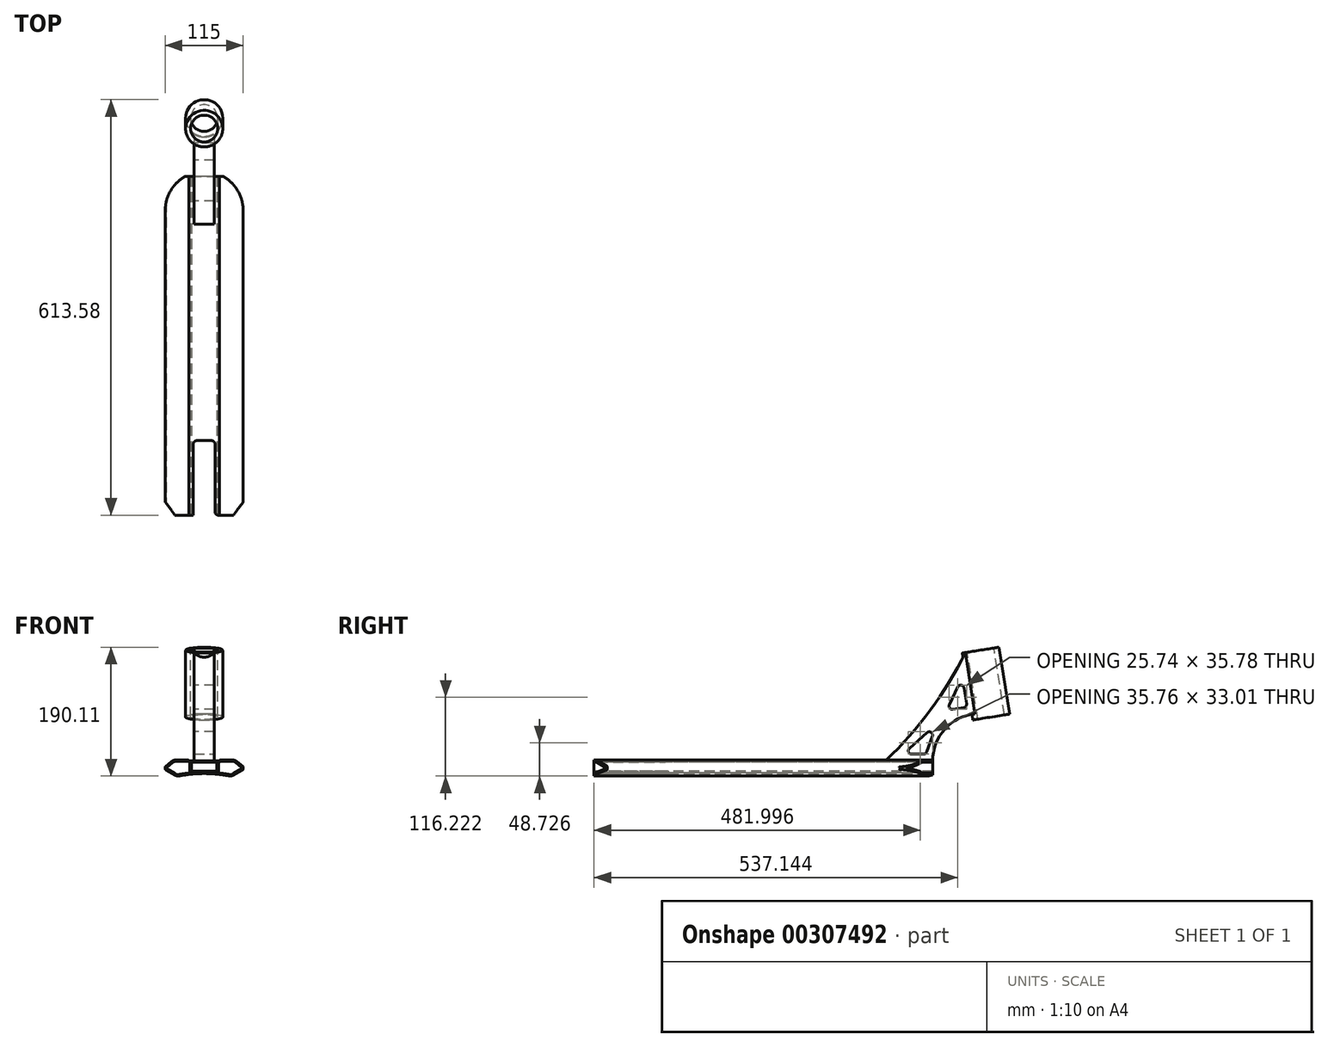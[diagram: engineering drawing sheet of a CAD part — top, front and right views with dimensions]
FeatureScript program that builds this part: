
annotation { "Feature Type Name" : "Feature", "Feature Type Description" : "" }
export const myFeature = defineFeature(function(context is Context, id is Id, definition is map)
    precondition{}
    {
        {
            var Q0;
            Q0=qCreatedBy(makeId("Front.planeOp"),FACE);
            var sketch = newSketch(context, id + "F0", { "sketchPlane" : qUnion([Q0])});
            skLineSegment(sketch, "E0", {"start": v(0, 0) * mm, "end": v(0, 24.16) * mm, "construction": true});
            skLineSegment(sketch, "E1", {"start": v(0, 0) * mm, "end": v(22.5, 0) * mm});
            skLineSegment(sketch, "E2", {"start": v(22.5, 0) * mm, "end": v(22.5, 1.3) * mm});
            skLineSegment(sketch, "E3", {"start": v(22.5, 1.3) * mm, "end": v(45.58, 1.3) * mm});
            skLineSegment(sketch, "E4", {"start": v(45.58, 1.3) * mm, "end": v(57.5, -8.7) * mm});
            skLineSegment(sketch, "E5", {"start": v(57.5, -8.7) * mm, "end": v(57.5, -12.7) * mm});
            skLineSegment(sketch, "E6", {"start": v(57.5, -12.7) * mm, "end": v(40.18, -22.7) * mm});
            skLineSegment(sketch, "E7.MirrorCS", {"start": v(0, 0) * mm, "end": v(-22.5, 0) * mm});
            skLineSegment(sketch, "E8.MirrorCS", {"start": v(-22.5, 1.3) * mm, "end": v(-45.58, 1.3) * mm});
            skLineSegment(sketch, "E9.MirrorCS", {"start": v(-22.5, 0) * mm, "end": v(-22.5, 1.3) * mm});
            skLineSegment(sketch, "E10.MirrorCS", {"start": v(-45.58, 1.3) * mm, "end": v(-57.5, -8.7) * mm});
            skLineSegment(sketch, "E11.MirrorCS", {"start": v(-57.5, -8.7) * mm, "end": v(-57.5, -12.7) * mm});
            skLineSegment(sketch, "E12.MirrorCS", {"start": v(-57.5, -12.7) * mm, "end": v(-40.18, -22.7) * mm});
            skArc(sketch, "E13", {"start": v(40.18, -22.7) * mm, "mid": v(0, -18.62) * mm, "end": v(-40.18, -22.7) * mm});
            skSolve(sketch);
        }
        {
            var Q0;
            Q0 = qSketchRegion(id + "F0", true);
            extrude(context, id + "F1", {"entities" : qUnion([Q0]), "endBound" : BoundingType.SYMMETRIC, "depth" : 500 * mm});
        }
        {
            var Q0;
            Q0=qCreatedBy(makeId("Front.planeOp"),FACE);
            var sketch = newSketch(context, id + "F2", { "sketchPlane" : qUnion([Q0])});
            skLineSegment(sketch, "E14.bottom", {"start": v(-19, -2) * mm, "end": v(19, -2) * mm});
            skLineSegment(sketch, "E14.top", {"start": v(-19, -15) * mm, "end": v(19, -15) * mm});
            skLineSegment(sketch, "E14.left", {"start": v(-19, -2) * mm, "end": v(-19, -15) * mm});
            skLineSegment(sketch, "E14.right", {"start": v(19, -2) * mm, "end": v(19, -15) * mm});
            skSolve(sketch);
        }
        {
            var Q0;
            Q0 = qSketchRegion(id + "F2", true);
            extrude(context, id + "F3", {"entities" : qUnion([Q0]), "operationType" : NewBodyOperationType.REMOVE, "endBound" : BoundingType.SYMMETRIC, "oppositeDirection" : true, "depth" : 500 * mm});
        }
        {
            var Q0;
            Q0=makeQuery(id+"F1.opExtrude","SWEPT_EDGE",EDGE,{"disambiguationData":[OSD([sQuery(id+"F0.wireOp",EDGE,"E8.MirrorCS"),sQuery(id+"F0.wireOp",EDGE,"E9.MirrorCS")])]});
            var Q1;
            Q1=makeQuery(id+"F1.opExtrude","SWEPT_EDGE",EDGE,{"disambiguationData":[OSD([sQuery(id+"F0.wireOp",EDGE,"E2"),sQuery(id+"F0.wireOp",EDGE,"E3")])]});
            fillet(context, id + "F4", {"entities" : qUnion([Q0, Q1]), "radius" : 2 * mm, "tangentPropagation" : true, "allowEdgeOverflow" : false});
        }
        {
            var Q0;
            Q0=makeQuery(id+"F1.opExtrude","SWEPT_EDGE",EDGE,{"disambiguationData":[OSD([sQuery(id+"F0.wireOp",EDGE,"E3"),sQuery(id+"F0.wireOp",EDGE,"E4")])]});
            var Q1;
            Q1=makeQuery(id+"F1.opExtrude","SWEPT_EDGE",EDGE,{"disambiguationData":[OSD([sQuery(id+"F0.wireOp",EDGE,"E6"),sQuery(id+"F0.wireOp",EDGE,"E13")])]});
            var Q2;
            Q2=makeQuery(id+"F1.opExtrude","SWEPT_EDGE",EDGE,{"disambiguationData":[OSD([sQuery(id+"F0.wireOp",EDGE,"E8.MirrorCS"),sQuery(id+"F0.wireOp",EDGE,"E10.MirrorCS")])]});
            var Q3;
            Q3=makeQuery(id+"F1.opExtrude","SWEPT_EDGE",EDGE,{"disambiguationData":[OSD([sQuery(id+"F0.wireOp",EDGE,"E12.MirrorCS"),sQuery(id+"F0.wireOp",EDGE,"E13")])]});
            fillet(context, id + "F5", {"entities" : qUnion([Q0, Q1, Q2, Q3]), "radius" : 9 * mm, "tangentPropagation" : true, "allowEdgeOverflow" : false});
        }
        {
            var Q0;
            Q0=makeQuery(id+"F1.opExtrude","SWEPT_EDGE",EDGE,{"disambiguationData":[OSD([sQuery(id+"F0.wireOp",EDGE,"E4"),sQuery(id+"F0.wireOp",EDGE,"E5")])]});
            var Q1;
            Q1=makeQuery(id+"F1.opExtrude","SWEPT_EDGE",EDGE,{"disambiguationData":[OSD([sQuery(id+"F0.wireOp",EDGE,"E5"),sQuery(id+"F0.wireOp",EDGE,"E6")])]});
            var Q2;
            Q2=makeQuery(id+"F1.opExtrude","SWEPT_EDGE",EDGE,{"disambiguationData":[OSD([sQuery(id+"F0.wireOp",EDGE,"E10.MirrorCS"),sQuery(id+"F0.wireOp",EDGE,"E11.MirrorCS")])]});
            var Q3;
            Q3=makeQuery(id+"F1.opExtrude","SWEPT_EDGE",EDGE,{"disambiguationData":[OSD([sQuery(id+"F0.wireOp",EDGE,"E11.MirrorCS"),sQuery(id+"F0.wireOp",EDGE,"E12.MirrorCS")])]});
            fillet(context, id + "F6", {"entities" : qUnion([Q0, Q1, Q2, Q3]), "radius" : 1 * mm, "tangentPropagation" : true, "allowEdgeOverflow" : false});
        }
        {
            var Q0;
            Q0=makeQuery(id+"F1.opExtrude","CAP_FACE",FACE,{"disambiguationData":[OSD([sQuery(id+"F0.wireOp",EDGE,"E1"),sQuery(id+"F0.wireOp",EDGE,"E2"),sQuery(id+"F0.wireOp",EDGE,"E3"),sQuery(id+"F0.wireOp",EDGE,"E4"),sQuery(id+"F0.wireOp",EDGE,"E5"),sQuery(id+"F0.wireOp",EDGE,"E6"),sQuery(id+"F0.wireOp",EDGE,"E7.MirrorCS"),sQuery(id+"F0.wireOp",EDGE,"E8.MirrorCS"),sQuery(id+"F0.wireOp",EDGE,"E9.MirrorCS"),sQuery(id+"F0.wireOp",EDGE,"E10.MirrorCS"),sQuery(id+"F0.wireOp",EDGE,"E11.MirrorCS"),sQuery(id+"F0.wireOp",EDGE,"E12.MirrorCS"),sQuery(id+"F0.wireOp",EDGE,"E13")])],"isStart":false});
            var sketch = newSketch(context, id + "F7", { "sketchPlane" : qUnion([Q0])});
            skArc(sketch, "E15.0", {"start": v(-37.3, -20.1) * mm, "mid": v(0, -16.62) * mm, "end": v(37.3, -20.1) * mm});
            skArc(sketch, "E15.1", {"start": v(-42.1, -19.28) * mm, "mid": v(-39.78, -20.12) * mm, "end": v(-37.3, -20.1) * mm});
            skLineSegment(sketch, "E15.2", {"start": v(-24.37, -0.7) * mm, "end": v(-42.3, -0.7) * mm});
            skArc(sketch, "E15.3", {"start": v(-42.3, -0.7) * mm, "mid": v(-44.7, -1.12) * mm, "end": v(-46.8, -2.34) * mm});
            skLineSegment(sketch, "E15.4", {"start": v(-46.8, -2.34) * mm, "end": v(-55.76, -9.85) * mm});
            skLineSegment(sketch, "E15.5", {"start": v(-55.61, -11.48) * mm, "end": v(-42.1, -19.28) * mm});
            skPoint(sketch, "E16.visualSharp", {"position": v(-56.85, -10.77) * mm});
            skArc(sketch, "E16.filletArc", {"start": v(-55.76, -9.85) * mm, "mid": v(-56.1, -10.7) * mm, "end": v(-55.61, -11.48) * mm});
            skLineSegment(sketch, "E17", {"start": v(-21, -17.72) * mm, "end": v(-21, -2) * mm});
            skLineSegment(sketch, "E18", {"start": v(-21, -2) * mm, "end": v(-22.5, -2) * mm});
            skArc(sketch, "E19", {"start": v(-22.5, -2) * mm, "mid": v(-23.23, -1.06) * mm, "end": v(-24.37, -0.7) * mm});
            skLineSegment(sketch, "E20.MirrorCS", {"start": v(55.61, -11.48) * mm, "end": v(42.1, -19.28) * mm});
            skArc(sketch, "E21.MirrorCS", {"start": v(42.1, -19.28) * mm, "mid": v(39.78, -20.12) * mm, "end": v(37.3, -20.1) * mm});
            skArc(sketch, "E22.MirrorCS", {"start": v(55.76, -9.85) * mm, "mid": v(56.1, -10.7) * mm, "end": v(55.61, -11.48) * mm});
            skLineSegment(sketch, "E23.MirrorCS", {"start": v(46.8, -2.34) * mm, "end": v(55.76, -9.85) * mm});
            skArc(sketch, "E24.MirrorCS", {"start": v(42.3, -0.7) * mm, "mid": v(44.7, -1.12) * mm, "end": v(46.8, -2.34) * mm});
            skLineSegment(sketch, "E25.MirrorCS", {"start": v(24.37, -0.7) * mm, "end": v(42.3, -0.7) * mm});
            skArc(sketch, "E26.MirrorCS", {"start": v(22.5, -2) * mm, "mid": v(23.23, -1.06) * mm, "end": v(24.37, -0.7) * mm});
            skLineSegment(sketch, "E27.MirrorCS", {"start": v(21, -2) * mm, "end": v(22.5, -2) * mm});
            skLineSegment(sketch, "E28.MirrorCS", {"start": v(21, -17.72) * mm, "end": v(21, -2) * mm});
            skArc(sketch, "E29.MirrorCS", {"start": v(37.3, -20.1) * mm, "mid": v(0, -16.62) * mm, "end": v(-37.3, -20.1) * mm});
            skPoint(sketch, "E30.0.15.end.orphan", {"position": v(-24.37, 1.3) * mm});
            skPoint(sketch, "E30.0.14.end.orphan", {"position": v(-22.5, 0) * mm});
            skPoint(sketch, "E30.0.13.end.orphan", {"position": v(22.5, 0) * mm});
            skPoint(sketch, "E30.0.12.end.orphan", {"position": v(24.37, 1.3) * mm});
            skPoint(sketch, "E30.0.11.end.orphan", {"position": v(42.3, 1.3) * mm});
            skPoint(sketch, "E30.0.10.end.orphan", {"position": v(48.1, -0.8) * mm});
            skPoint(sketch, "E30.0.9.end.orphan", {"position": v(57.14, -8.4) * mm});
            skPoint(sketch, "E30.0.8.end.orphan", {"position": v(57.5, -9.17) * mm});
            skPoint(sketch, "E30.0.7.end.orphan", {"position": v(57.5, -12.12) * mm});
            skPoint(sketch, "E30.0.6.end.orphan", {"position": v(57, -12.99) * mm});
            skPoint(sketch, "E30.0.5.end.orphan", {"position": v(43.1, -21.01) * mm});
            skPoint(sketch, "E30.0.4.end.orphan", {"position": v(36.94, -22.06) * mm});
            skPoint(sketch, "E30.0.3.end.orphan", {"position": v(-36.94, -22.06) * mm});
            skPoint(sketch, "E30.0.2.end.orphan", {"position": v(-43.1, -21.01) * mm});
            skPoint(sketch, "E30.0.1.end.orphan", {"position": v(-57, -12.99) * mm});
            skPoint(sketch, "E30.0.0.end.orphan", {"position": v(-57.5, -12.12) * mm});
            skPoint(sketch, "E30.0.19.end.orphan", {"position": v(-57.5, -9.17) * mm});
            skPoint(sketch, "E30.0.18.end.orphan", {"position": v(-57.14, -8.4) * mm});
            skPoint(sketch, "E30.0.17.end.orphan", {"position": v(-48.1, -0.8) * mm});
            skPoint(sketch, "E30.0.17.start.orphan", {"position": v(-42.3, 1.3) * mm});
            skSolve(sketch);
        }
        {
            var Q0;
            Q0=makeQuery(id+"F7.imprint","IMPRINT",FACE,{"disambiguationData":[TD([[makeQuery(id+"F7.imprint","IMPRINT",EDGE,{"derivedFrom":sQuery(id+"F7.wireOp",EDGE,"E20.MirrorCS")}),-1.0]])]});
            var Q1;
            {var subQ0=sQuery(id+"F7.wireOp",EDGE,"E15.1");Q1=makeQuery(id+"F7.imprint","IMPRINT",FACE,{"disambiguationData":[TD([[makeQuery(id+"F7.imprint","IMPRINT",EDGE,{"derivedFrom":subQ0}),1.0]])]});}
            extrude(context, id + "F8", {"entities" : qUnion([Q0, Q1]), "operationType" : NewBodyOperationType.REMOVE, "endBound" : BoundingType.THROUGH_ALL, "oppositeDirection" : true, "depth" : 25 * mm});
        }
        {
            var Q0;
            Q0=qCreatedBy(makeId("Top.planeOp"),FACE);
            var sketch = newSketch(context, id + "F9", { "sketchPlane" : qUnion([Q0])});
            skArc(sketch, "E31", {"start": v(57.5, 200) * mm, "mid": v(0, 257.5) * mm, "end": v(-57.5, 200) * mm});
            skLineSegment(sketch, "E32", {"start": v(-57.5, 200) * mm, "end": v(-57.5, 280) * mm});
            skLineSegment(sketch, "E33", {"start": v(57.5, 200) * mm, "end": v(57.5, 280) * mm});
            skLineSegment(sketch, "E34", {"start": v(-57.5, 280) * mm, "end": v(57.5, 280) * mm});
            skSolve(sketch);
        }
        {
            var Q0;
            Q0 = qSketchRegion(id + "F9", true);
            extrude(context, id + "F10", {"entities" : qUnion([Q0]), "operationType" : NewBodyOperationType.ADD, "depth" : 25 * mm});
        }
        {
            var Q0;
            Q0 = qSketchRegion(id + "F9", true);
            extrude(context, id + "F11", {"entities" : qUnion([Q0]), "operationType" : NewBodyOperationType.REMOVE, "endBound" : BoundingType.THROUGH_ALL, "oppositeDirection" : true, "depth" : 25 * mm, "hasSecondDirection" : true, "secondDirectionBound" : SecondDirectionBoundingType.THROUGH_ALL, "secondDirectionOppositeDirection" : false, "secondDirectionDepth" : 25 * mm});
        }
        {
            var Q0;
            Q0=qCreatedBy(makeId("Top.planeOp"),FACE);
            var sketch = newSketch(context, id + "F12", { "sketchPlane" : qUnion([Q0])});
            skLineSegment(sketch, "E35", {"start": v(-68, -216) * mm, "end": v(-43.3, -250) * mm});
            skLineSegment(sketch, "E36", {"start": v(-43.3, -250) * mm, "end": v(-16, -250) * mm});
            skLineSegment(sketch, "E37", {"start": v(-16, -250) * mm, "end": v(-16, -140) * mm});
            skLineSegment(sketch, "E38", {"start": v(-16, -140) * mm, "end": v(16, -140) * mm});
            skLineSegment(sketch, "E39", {"start": v(16, -140) * mm, "end": v(16, -250) * mm});
            skLineSegment(sketch, "E40", {"start": v(16, -250) * mm, "end": v(43.3, -250) * mm});
            skLineSegment(sketch, "E41", {"start": v(43.3, -250) * mm, "end": v(68, -216) * mm});
            skLineSegment(sketch, "E42", {"start": v(68, -216) * mm, "end": v(68, -346) * mm});
            skLineSegment(sketch, "E43", {"start": v(68, -346) * mm, "end": v(-68, -346) * mm});
            skLineSegment(sketch, "E44", {"start": v(-68, -346) * mm, "end": v(-68, -216) * mm});
            skSolve(sketch);
        }
        {
            var Q0;
            Q0 = qSketchRegion(id + "F12", true);
            extrude(context, id + "F13", {"entities" : qUnion([Q0]), "operationType" : NewBodyOperationType.REMOVE, "endBound" : BoundingType.THROUGH_ALL, "oppositeDirection" : true, "depth" : 25 * mm, "hasSecondDirection" : true, "secondDirectionBound" : SecondDirectionBoundingType.THROUGH_ALL, "secondDirectionOppositeDirection" : false, "secondDirectionDepth" : 25 * mm});
        }
        {
            var Q0;
            {var subQ0=sQuery(id+"F12.wireOp",EDGE,"E38");var subQ1=sQuery(id+"F12.wireOp",EDGE,"E37");Q0=makeQuery(id+"F13.boolean.opBoolean","COPY",EDGE,{"disambiguationData":[TD([makeQuery(id+"F1.opExtrude","SWEPT_FACE",FACE,{"disambiguationData":[OSD([sQuery(id+"F0.wireOp",EDGE,"E13")])]})])],"derivedFrom":makeQuery(id+"F13.opExtrude","SWEPT_EDGE",EDGE,{"disambiguationData":[OSD([subQ1,subQ0])]})});}
            var Q1;
            {var subQ0=sQuery(id+"F12.wireOp",EDGE,"E37");var subQ1=sQuery(id+"F12.wireOp",EDGE,"E38");Q1=makeQuery(id+"F13.boolean.opBoolean","COPY",EDGE,{"disambiguationData":[TD([makeQuery(id+"F3.boolean.opBoolean","COPY",FACE,{"derivedFrom":makeQuery(id+"F3.opExtrude","SWEPT_FACE",FACE,{"disambiguationData":[OSD([sQuery(id+"F2.wireOp",EDGE,"E14.bottom")])]})})])],"derivedFrom":makeQuery(id+"F13.opExtrude","SWEPT_EDGE",EDGE,{"disambiguationData":[OSD([subQ0,subQ1])]})});}
            var Q2;
            {var subQ0=sQuery(id+"F12.wireOp",EDGE,"E38");var subQ1=sQuery(id+"F12.wireOp",EDGE,"E39");Q2=makeQuery(id+"F13.boolean.opBoolean","COPY",EDGE,{"disambiguationData":[TD([makeQuery(id+"F1.opExtrude","SWEPT_FACE",FACE,{"disambiguationData":[OSD([sQuery(id+"F0.wireOp",EDGE,"E13")])]})])],"derivedFrom":makeQuery(id+"F13.opExtrude","SWEPT_EDGE",EDGE,{"disambiguationData":[OSD([subQ0,subQ1])]})});}
            var Q3;
            {var subQ0=sQuery(id+"F12.wireOp",EDGE,"E38");var subQ1=sQuery(id+"F12.wireOp",EDGE,"E39");Q3=makeQuery(id+"F13.boolean.opBoolean","COPY",EDGE,{"disambiguationData":[TD([makeQuery(id+"F3.boolean.opBoolean","COPY",FACE,{"derivedFrom":makeQuery(id+"F3.opExtrude","SWEPT_FACE",FACE,{"disambiguationData":[OSD([sQuery(id+"F2.wireOp",EDGE,"E14.bottom")])]})})])],"derivedFrom":makeQuery(id+"F13.opExtrude","SWEPT_EDGE",EDGE,{"disambiguationData":[OSD([subQ0,subQ1])]})});}
            var Q4;
            {var subQ2=sQuery(id+"F12.wireOp",EDGE,"E39");Q4=makeQuery(id+"F13.boolean.opBoolean","COPY",EDGE,{"disambiguationData":[TD([makeQuery(id+"F3.boolean.opBoolean","COPY",FACE,{"derivedFrom":makeQuery(id+"F3.opExtrude","SWEPT_FACE",FACE,{"disambiguationData":[OSD([sQuery(id+"F2.wireOp",EDGE,"E14.bottom")])]})})])],"derivedFrom":makeQuery(id+"F13.opExtrude","SWEPT_EDGE",EDGE,{"disambiguationData":[OSD([subQ2,sQuery(id+"F12.wireOp",EDGE,"E40")])]})});}
            var Q5;
            {var subQ2=sQuery(id+"F12.wireOp",EDGE,"E37");Q5=makeQuery(id+"F13.boolean.opBoolean","COPY",EDGE,{"disambiguationData":[TD([makeQuery(id+"F3.boolean.opBoolean","COPY",FACE,{"derivedFrom":makeQuery(id+"F3.opExtrude","SWEPT_FACE",FACE,{"disambiguationData":[OSD([sQuery(id+"F2.wireOp",EDGE,"E14.bottom")])]})})])],"derivedFrom":makeQuery(id+"F13.opExtrude","SWEPT_EDGE",EDGE,{"disambiguationData":[OSD([sQuery(id+"F12.wireOp",EDGE,"E36"),subQ2])]})});}
            fillet(context, id + "F14", {"entities" : qUnion([Q0, Q1, Q2, Q3, Q4, Q5]), "radius" : 5 * mm, "tangentPropagation" : true, "allowEdgeOverflow" : false});
        }
        {
            var Q0;
            Q0=qCreatedBy(makeId("Right.planeOp"),FACE);
            var sketch = newSketch(context, id + "F15", { "sketchPlane" : qUnion([Q0])});
            skLineSegment(sketch, "E45", {"start": v(180, 0) * mm, "end": v(250, 0) * mm});
            skArc(sketch, "E46", {"start": v(180, 0) * mm, "mid": v(246.34, 74.62) * mm, "end": v(298.1, 160) * mm});
            skLineSegment(sketch, "E47", {"start": v(298.1, 160) * mm, "end": v(343.53, 167.2) * mm});
            skArc(sketch, "E48", {"start": v(312.42, 69.59) * mm, "mid": v(267.9, 46.74) * mm, "end": v(250, 0) * mm});
            skLineSegment(sketch, "E49", {"start": v(312.42, 69.59) * mm, "end": v(313.74, 61.23) * mm});
            skLineSegment(sketch, "E50", {"start": v(313.74, 61.23) * mm, "end": v(359.18, 68.43) * mm});
            skLineSegment(sketch, "E51", {"start": v(343.53, 167.2) * mm, "end": v(359.18, 68.43) * mm});
            skSolve(sketch);
        }
        {
            var Q0;
            Q0 = qSketchRegion(id + "F15", true);
            extrude(context, id + "F16", {"entities" : qUnion([Q0]), "operationType" : NewBodyOperationType.ADD, "endBound" : BoundingType.SYMMETRIC, "depth" : 30 * mm});
        }
        {
            var Q0;
            Q0=makeQuery(id+"F16.opExtrude","SWEPT_FACE",FACE,{"disambiguationData":[OSD([sQuery(id+"F15.wireOp",EDGE,"E47")])]});
            var sketch = newSketch(context, id + "F17", { "sketchPlane" : qUnion([Q0])});
            skCircle(sketch, "E52", {"center": v(0, 342.46) * mm, "radius": 27.46 * mm});
            skSolve(sketch);
        }
        {
            var Q0;
            Q0 = qSketchRegion(id + "F17", true);
            var Q1;
            Q1=makeQuery(id+"F16.opExtrude","SWEPT_FACE",FACE,{"disambiguationData":[OSD([sQuery(id+"F15.wireOp",EDGE,"E50")])]});
            extrude(context, id + "F18", {"entities" : qUnion([Q0]), "operationType" : NewBodyOperationType.ADD, "endBound" : BoundingType.UP_TO_SURFACE, "oppositeDirection" : true, "endBoundEntityFace" : qUnion([Q1]), "depth" : 25 * mm});
        }
        {
            var Q0;
            Q0=makeQuery(id+"F18.boolean.opBoolean","MERGE",FACE,{"derivedFrom":[makeQuery(id+"F16.opExtrude","SWEPT_FACE",FACE,{"disambiguationData":[OSD([sQuery(id+"F15.wireOp",EDGE,"E47")])]}),makeQuery(id+"F18.opExtrude","CAP_FACE",FACE,{"disambiguationData":[OSD([sQuery(id+"F17.wireOp",EDGE,"E52")])],"isStart":true})]});
            var sketch = newSketch(context, id + "F19", { "sketchPlane" : qUnion([Q0])});
            skPoint(sketch, "E53", {"position": v(0, 342.46) * mm});
            skSolve(sketch);
        }
        {
            var Q0;
            Q0=sQuery(id+"F19.wireOp",VERTEX,"E53");
            var Q1;
            Q1=makeQuery(id+"F1.opExtrude","SWEPT_BODY",BODY,{"disambiguationData":[OSD([sQuery(id+"F0.wireOp",EDGE,"E1"),sQuery(id+"F0.wireOp",EDGE,"E2"),sQuery(id+"F0.wireOp",EDGE,"E3"),sQuery(id+"F0.wireOp",EDGE,"E4"),sQuery(id+"F0.wireOp",EDGE,"E5"),sQuery(id+"F0.wireOp",EDGE,"E6"),sQuery(id+"F0.wireOp",EDGE,"E7.MirrorCS"),sQuery(id+"F0.wireOp",EDGE,"E8.MirrorCS"),sQuery(id+"F0.wireOp",EDGE,"E9.MirrorCS"),sQuery(id+"F0.wireOp",EDGE,"E10.MirrorCS"),sQuery(id+"F0.wireOp",EDGE,"E11.MirrorCS"),sQuery(id+"F0.wireOp",EDGE,"E12.MirrorCS"),sQuery(id+"F0.wireOp",EDGE,"E13")])]});
            hole(context, id + "F20", {"style" : HoleStyle.SIMPLE, "endStyle" : HoleEndStyle.THROUGH, "holeDiameter" : 40 * mm, "isTappedThrough" : true, "tappedDepth" : 12 * mm, "tapClearance" : 3, "locations" : qUnion([Q0]), "scope" : qUnion([Q1])});
        }
        {
            var Q0;
            Q0=makeQuery(id+"F16.opExtrude","CAP_FACE",FACE,{"disambiguationData":[OSD([sQuery(id+"F15.wireOp",EDGE,"E45"),sQuery(id+"F15.wireOp",EDGE,"E46"),sQuery(id+"F15.wireOp",EDGE,"E47"),sQuery(id+"F15.wireOp",EDGE,"E48"),sQuery(id+"F15.wireOp",EDGE,"E49"),sQuery(id+"F15.wireOp",EDGE,"E50"),sQuery(id+"F15.wireOp",EDGE,"E51")])],"isStart":false});
            var sketch = newSketch(context, id + "F21", { "sketchPlane" : qUnion([Q0])});
            skLineSegment(sketch, "E54", {"start": v(293.7, 123.87) * mm, "end": v(270.74, 74.67) * mm});
            skLineSegment(sketch, "E55", {"start": v(270.74, 74.67) * mm, "end": v(300.74, 79.42) * mm});
            skLineSegment(sketch, "E56", {"start": v(300.74, 79.42) * mm, "end": v(293.7, 123.87) * mm});
            skLineSegment(sketch, "E57", {"start": v(256.38, 55) * mm, "end": v(240, 10) * mm});
            skLineSegment(sketch, "E58", {"start": v(240, 10) * mm, "end": v(206, 10) * mm});
            skLineSegment(sketch, "E59", {"start": v(206, 10) * mm, "end": v(256.38, 55) * mm});
            skSolve(sketch);
        }
        {
            var Q0;
            Q0=makeQuery(id+"F21.imprint","IMPRINT",FACE,{"disambiguationData":[TD([[makeQuery(id+"F21.imprint","IMPRINT",EDGE,{"derivedFrom":sQuery(id+"F21.wireOp",EDGE,"E57")}),-1.0]])]});
            var Q1;
            Q1=makeQuery(id+"F21.imprint","IMPRINT",FACE,{"disambiguationData":[TD([[makeQuery(id+"F21.imprint","IMPRINT",EDGE,{"derivedFrom":sQuery(id+"F21.wireOp",EDGE,"E54")}),1.0]])]});
            extrude(context, id + "F22", {"entities" : qUnion([Q0, Q1]), "operationType" : NewBodyOperationType.REMOVE, "endBound" : BoundingType.THROUGH_ALL, "oppositeDirection" : true, "depth" : 25 * mm});
        }
        {
            var Q0;
            Q0=makeQuery(id+"F22.boolean.opBoolean","COPY",EDGE,{"derivedFrom":makeQuery(id+"F22.opExtrude","SWEPT_EDGE",EDGE,{"disambiguationData":[OSD([sQuery(id+"F21.wireOp",EDGE,"E57"),sQuery(id+"F21.wireOp",EDGE,"E58")])]})});
            var Q1;
            Q1=makeQuery(id+"F22.boolean.opBoolean","COPY",EDGE,{"derivedFrom":makeQuery(id+"F22.opExtrude","SWEPT_EDGE",EDGE,{"disambiguationData":[OSD([sQuery(id+"F21.wireOp",EDGE,"E55"),sQuery(id+"F21.wireOp",EDGE,"E56")])]})});
            var Q2;
            Q2=makeQuery(id+"F22.boolean.opBoolean","COPY",EDGE,{"derivedFrom":makeQuery(id+"F22.opExtrude","SWEPT_EDGE",EDGE,{"disambiguationData":[OSD([sQuery(id+"F21.wireOp",EDGE,"E54"),sQuery(id+"F21.wireOp",EDGE,"E56")])]})});
            var Q3;
            Q3=makeQuery(id+"F22.boolean.opBoolean","COPY",EDGE,{"derivedFrom":makeQuery(id+"F22.opExtrude","SWEPT_EDGE",EDGE,{"disambiguationData":[OSD([sQuery(id+"F21.wireOp",EDGE,"E54"),sQuery(id+"F21.wireOp",EDGE,"E55")])]})});
            var Q4;
            Q4=makeQuery(id+"F22.boolean.opBoolean","COPY",EDGE,{"derivedFrom":makeQuery(id+"F22.opExtrude","SWEPT_EDGE",EDGE,{"disambiguationData":[OSD([sQuery(id+"F21.wireOp",EDGE,"E58"),sQuery(id+"F21.wireOp",EDGE,"E59")])]})});
            var Q5;
            Q5=makeQuery(id+"F22.boolean.opBoolean","COPY",EDGE,{"derivedFrom":makeQuery(id+"F22.opExtrude","SWEPT_EDGE",EDGE,{"disambiguationData":[OSD([sQuery(id+"F21.wireOp",EDGE,"E57"),sQuery(id+"F21.wireOp",EDGE,"E59")])]})});
            fillet(context, id + "F23", {"entities" : qUnion([Q0, Q1, Q2, Q3, Q4, Q5]), "radius" : 5 * mm, "tangentPropagation" : true, "allowEdgeOverflow" : false});
        }
    });
